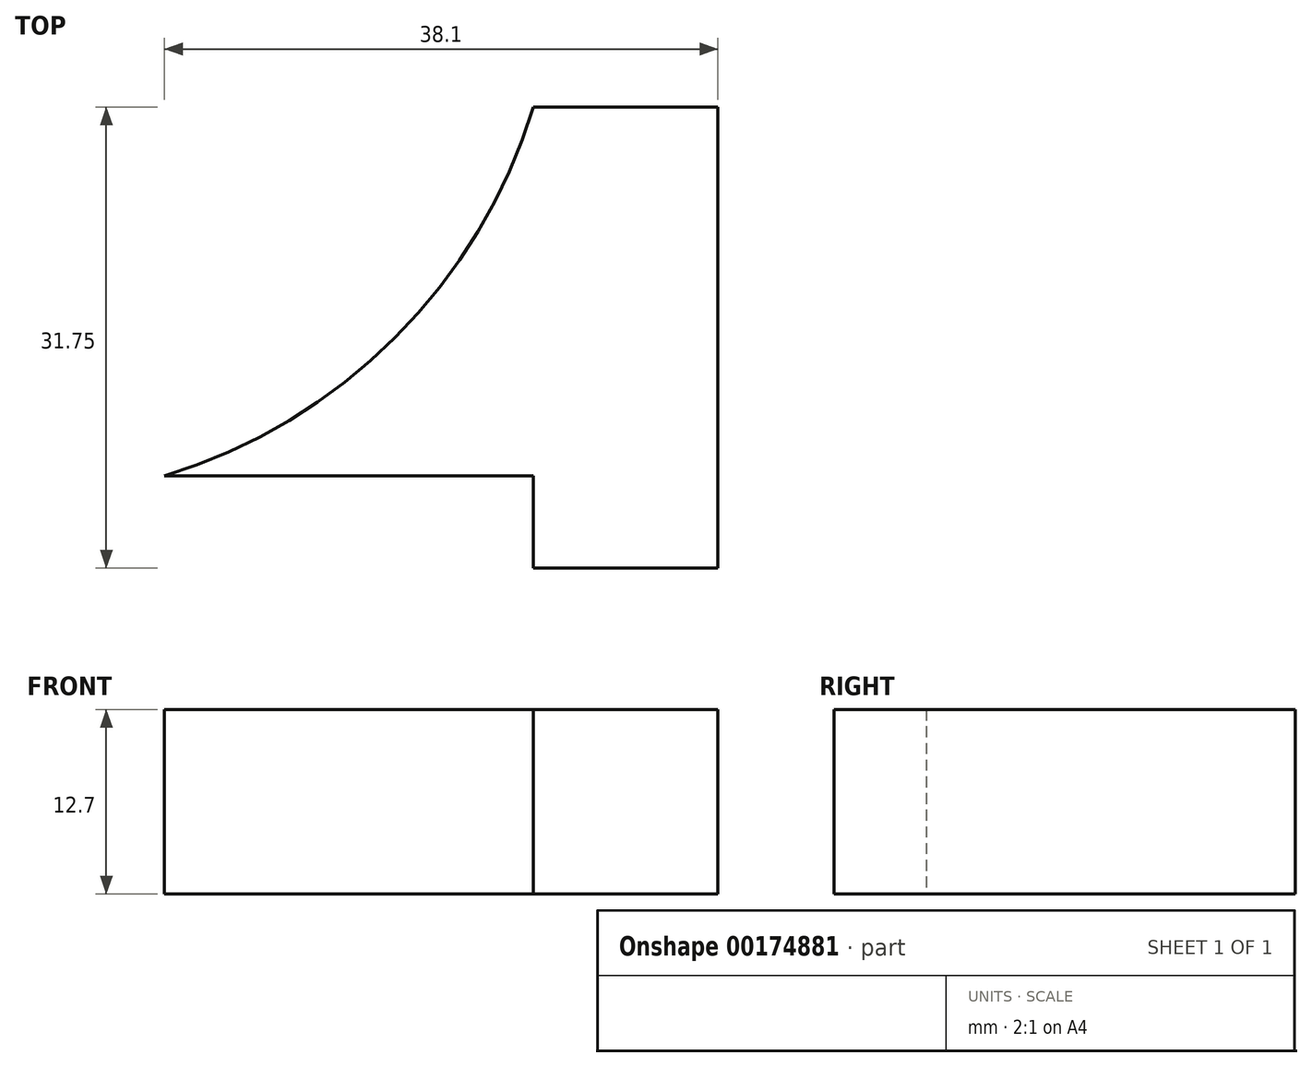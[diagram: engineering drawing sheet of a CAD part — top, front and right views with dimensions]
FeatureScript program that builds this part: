
annotation { "Feature Type Name" : "Feature", "Feature Type Description" : "" }
export const myFeature = defineFeature(function(context is Context, id is Id, definition is map)
    precondition{}
    {
        {
            var Q0;
            Q0=qCreatedBy(makeId("Top.planeOp"),FACE);
            var sketch = newSketch(context, id + "F0", { "sketchPlane" : qUnion([Q0])});
            skLineSegment(sketch, "E0", {"start": v(0, 25.4) * mm, "end": v(0, 0) * mm});
            skLineSegment(sketch, "E1", {"start": v(0, 0) * mm, "end": v(-25.4, 0) * mm});
            skArc(sketch, "E2", {"start": v(-25.4, 0) * mm, "mid": v(-9.52, 9.52) * mm, "end": v(0, 25.4) * mm});
            skLineSegment(sketch, "E3.bottom", {"start": v(-25.4, 0) * mm, "end": v(0, 0) * mm});
            skLineSegment(sketch, "E3.top", {"start": v(-25.4, -6.35) * mm, "end": v(0, -6.35) * mm});
            skLineSegment(sketch, "E3.left", {"start": v(-25.4, 0) * mm, "end": v(-25.4, -6.35) * mm});
            skLineSegment(sketch, "E3.right", {"start": v(0, 0) * mm, "end": v(0, -6.35) * mm});
            skLineSegment(sketch, "E4.bottom", {"start": v(0, 25.4) * mm, "end": v(12.7, 25.4) * mm});
            skLineSegment(sketch, "E4.top", {"start": v(0, -6.35) * mm, "end": v(12.7, -6.35) * mm});
            skLineSegment(sketch, "E4.left", {"start": v(0, 25.4) * mm, "end": v(0, -6.35) * mm});
            skLineSegment(sketch, "E4.right", {"start": v(12.7, 25.4) * mm, "end": v(12.7, -6.35) * mm});
            skSolve(sketch);
        }
        {
            var Q0;
            {var subQ0=sQuery(id+"F0.wireOp",EDGE,"E2");Q0=makeQuery(id+"F0.imprint","IMPRINT",FACE,{"disambiguationData":[TD([[makeQuery(id+"F0.imprint","IMPRINT",EDGE,{"derivedFrom":subQ0}),-1.0]])]});}
            var Q1;
            {var subQ3=sQuery(id+"F0.wireOp",EDGE,"E4.bottom");Q1=makeQuery(id+"F0.imprint","IMPRINT",FACE,{"disambiguationData":[TD([[makeQuery(id+"F0.imprint","IMPRINT",EDGE,{"derivedFrom":subQ3}),-1.0]])]});}
            var Q2;
            {var subQ0=sQuery(id+"F0.wireOp",EDGE,"E3.bottom");Q2=makeQuery(id+"F0.imprint","IMPRINT",FACE,{"disambiguationData":[TD([[makeQuery(id+"F0.imprint","IMPRINT",EDGE,{"derivedFrom":subQ0}),-1.0]])]});}
            extrude(context, id + "F1", {"entities" : qUnion([Q0, Q1, Q2]), "depth" : 12.7 * mm});
        }
    });
